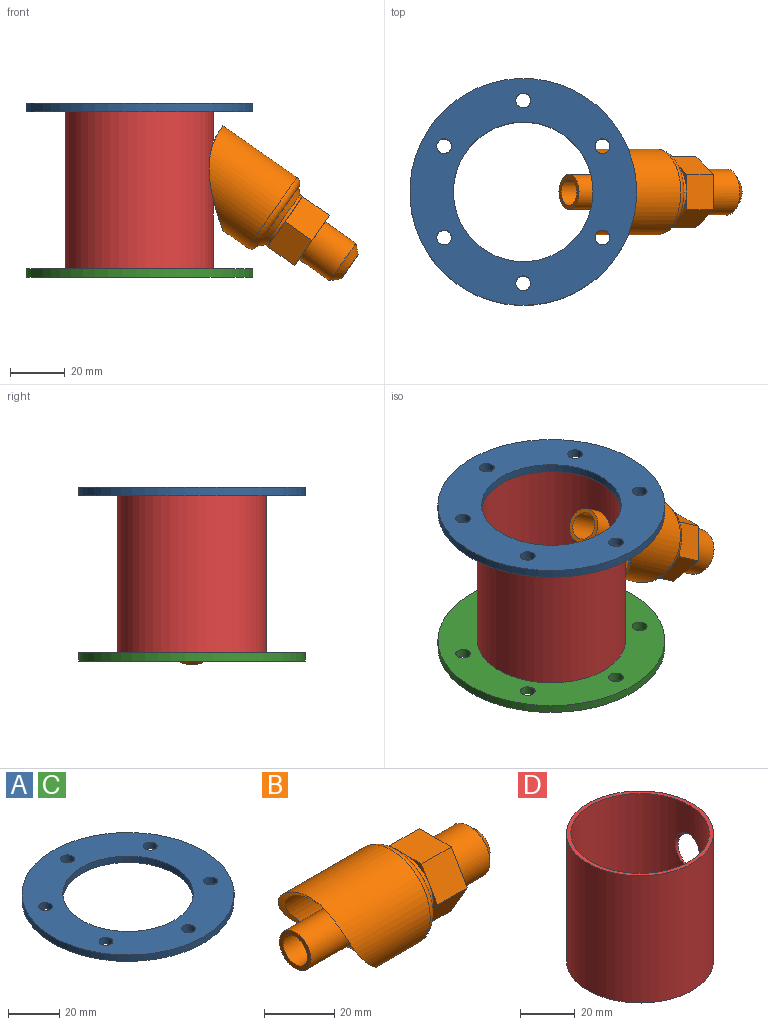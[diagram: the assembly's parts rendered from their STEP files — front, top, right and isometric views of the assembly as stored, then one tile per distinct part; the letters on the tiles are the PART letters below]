
ASSEMBLY  parts=4 mates=5
PART A: 10 faces, bbox 82.6x82.6x3 mm
  f0: cylinder r=25.4mm len=50.8mm, axis (0,0,-1), area 486.4mm2, adj f8,f9
  f1: cylinder r=2.68mm len=5.36mm, axis (0,0,-1), area 51.3mm2, adj f8,f9
  f2: cylinder r=2.68mm len=5.36mm, axis (0,0,-1), area 51.3mm2, adj f8,f9
  f3: cylinder r=2.68mm len=5.36mm, axis (0,0,-1), area 51.3mm2, adj f8,f9
  f4: cylinder r=2.68mm len=5.36mm, axis (0,0,-1), area 51.3mm2, adj f8,f9
  f5: cylinder r=2.68mm len=5.36mm, axis (0,0,-1), area 51.3mm2, adj f8,f9
  f6: cylinder r=2.68mm len=5.36mm, axis (0,0,-1), area 51.3mm2, adj f8,f9
  f7: cylinder r=41.27mm len=82.55mm, axis (0,0,-1), area 790.5mm2, adj f8,f9
  f8: plane 82.55x82.55mm, normal (0,0,1), area 3189.9mm2, adj f0,f1,f2,f3,f4,f5,f6,f7
  f9: plane 82.55x82.55mm, normal (0,0,-1), area 3189.9mm2, adj f0,f1,f2,f3,f4,f5,f6,f7
PART B: 26 faces, bbox 73.2x33.8x35.4 mm
  f0: cylinder r=15.62mm len=32.89mm, axis (-1,0,0), area 2445.4mm2, adj f3,f21
  f1: cylinder r=4.89mm len=73.15mm, axis (-1,0,0), area 2247.3mm2, adj f19,f25
  f2: cylinder r=11.11mm len=22.23mm, axis (1,0,0), area 79.8mm2, adj f4,f5,f6,f7,f8,f9,f10
  f3: torus R=13.08mm, axis (1,0,0), area 365.6mm2, adj f0,f4
  f4: cone r=11.11mm half-angle=44.6deg, axis (-1,0,0), area 217.2mm2, adj f2,f3
  f5: plane 9.62x5.56mm, normal (-1,0,0), area 6.6mm2, adj f2,f12,f13
  f6: plane 9.62x5.56mm, normal (-1,0,0), area 6.6mm2, adj f2,f13,f14
  f7: plane 11.11x3.21mm, normal (-1,0,0), area 6.6mm2, adj f2,f14,f15
  f8: plane 9.62x5.56mm, normal (-1,0,0), area 6.6mm2, adj f2,f15,f16
  f9: plane 9.62x5.56mm, normal (-1,0,0), area 6.6mm2, adj f2,f11,f16
  f10: plane 11.11x3.21mm, normal (-1,0,0), area 6.6mm2, adj f2,f11,f12
  f11: plane 11.94x11.11mm, normal (0,0.87,-0.5), area 153.2mm2, adj f9,f10,f12,f16,f17
  f12: plane 11.94x11.11mm, normal (0,0.87,0.5), area 153.2mm2, adj f5,f10,f11,f13,f17
  f13: plane 12.83x11.94mm, normal (0,0,1), area 153.2mm2, adj f5,f6,f12,f14,f17
  f14: plane 11.94x11.11mm, normal (0,-0.87,0.5), area 153.2mm2, adj f6,f7,f13,f15,f17
  f15: plane 11.94x11.11mm, normal (0,-0.87,-0.5), area 153.2mm2, adj f7,f8,f14,f16,f17
  f16: plane 12.83x11.94mm, normal (0,0,-1), area 153.2mm2, adj f8,f9,f11,f15,f17
  f17: plane 25.66x22.23mm, normal (1,0,0), area 209.7mm2, adj f11,f12,f13,f14,f15,f16,f18
  f18: cylinder r=8.33mm len=16.66mm, axis (-1,0,0), area 718mm2, adj f17,f20
  f19: plane 10.57x10.57mm, normal (1,0,0), area 12.6mm2, adj f1,f20
  f20: cone r=5.28mm half-angle=45deg, axis (-1,0,0), area 184.4mm2, adj f18,f19
  f21: cylinder r=26.99mm len=34.1mm, axis (-0.57,0,0.82), area 189.1mm2, adj f0,f24
  f22: cylinder r=6.35mm len=40.13mm, axis (-1,0,0), area 1601.2mm2, adj f23,f25
  f23: plane 28.19x28.19mm, normal (-1,0,0), area 497.6mm2, adj f22,f24
  f24: cylinder r=14.1mm len=33.22mm, axis (-1,0,0), area 2279.3mm2, adj f21,f23
  f25: plane 12.7x12.7mm, normal (-1,0,0), area 51.6mm2, adj f1,f22
PART C: same geometry as A
PART D: 5 faces, bbox 61.3x54x57.2 mm
  f0: cylinder r=25.4mm len=57.15mm, axis (0,0,-1), area 8965mm2, adj f2,f3,f4
  f1: cylinder r=26.99mm len=57.15mm, axis (0,0,-1), area 9535mm2, adj f2,f3,f4
  f2: plane 53.98x53.98mm, normal (0,0,1), area 261.3mm2, adj f0,f1
  f3: plane 53.98x53.98mm, normal (0,0,-1), area 261.3mm2, adj f0,f1
  f4: cylinder r=6.35mm len=16.62mm, axis (0.82,0,-0.57), area 78.5mm2, adj f0,f1
PLACE A t=(-13.69,51.37,29.2)mm
PLACE B rot(axis=(0,1,0),35deg) t=(2.96,51.37,14.65)mm
PLACE C t=(-13.69,51.37,-31)mm
PLACE D t=(-13.69,51.37,-27.95)mm
MATE fastened C.f0 <-> D.f0  axis (0,0,1) through (-13.69,51.37,-27.95)mm
MATE cylindrical B.f0 <-> D.f4  axis (-0.82,0,0.57) through (2.96,51.37,14.65)mm
MATE cylindrical A.f0 <-> D.f0  axis (0,0,-1) through (-13.69,51.37,30.72)mm
MATE cylindrical C.f0 <-> D.f0  axis (0,0,-1) through (-13.69,51.37,-29.47)mm
MATE fastened A.f0 <-> D.f0  axis (0,0,-1) through (-13.69,51.37,29.2)mm
